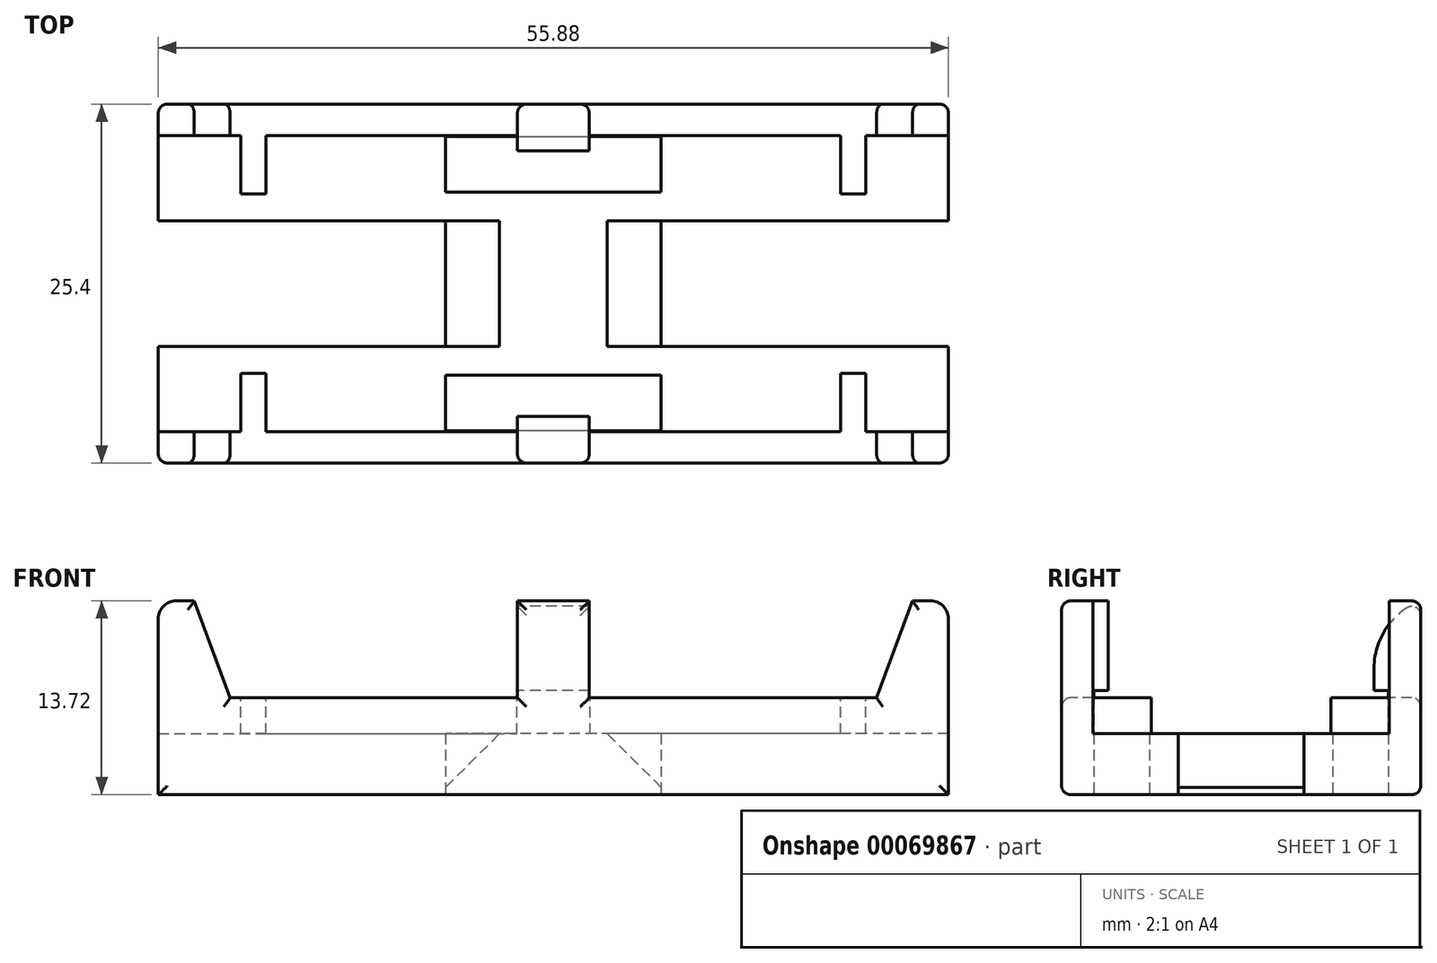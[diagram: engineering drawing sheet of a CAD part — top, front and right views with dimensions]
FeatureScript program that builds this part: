
annotation { "Feature Type Name" : "Feature", "Feature Type Description" : "" }
export const myFeature = defineFeature(function(context is Context, id is Id, definition is map)
    precondition{}
    {
        {
            var Q0;
            Q0=qCreatedBy(makeId("Top.planeOp"),FACE);
            var sketch = newSketch(context, id + "F0", { "sketchPlane" : qUnion([Q0])});
            skLineSegment(sketch, "E0.bottom", {"start": v(-27.94, 12.7) * mm, "end": v(27.94, 12.7) * mm});
            skLineSegment(sketch, "E0.top", {"start": v(-27.94, -12.7) * mm, "end": v(27.94, -12.7) * mm});
            skLineSegment(sketch, "E0.left", {"start": v(-27.94, 12.7) * mm, "end": v(-27.94, -12.7) * mm});
            skLineSegment(sketch, "E0.right", {"start": v(27.94, 12.7) * mm, "end": v(27.94, -12.7) * mm});
            skPoint(sketch, "E0.middle", {"position": v(0, 0) * mm});
            skSolve(sketch);
        }
        {
            var Q0;
            Q0=makeQuery(id+"F0.imprint","IMPRINT",FACE,{"disambiguationData":[TD([[makeQuery(id+"F0.imprint","IMPRINT",EDGE,{"derivedFrom":sQuery(id+"F0.wireOp",EDGE,"E0.bottom")}),-1.0]])]});
            extrude(context, id + "F1", {"entities" : qUnion([Q0]), "depth" : 13.72 * mm});
        }
        {
            var Q0;
            Q0=makeQuery(id+"F1.opExtrude","CAP_FACE",FACE,{"disambiguationData":[OSD([sQuery(id+"F0.wireOp",EDGE,"E0.bottom"),sQuery(id+"F0.wireOp",EDGE,"E0.top"),sQuery(id+"F0.wireOp",EDGE,"E0.left"),sQuery(id+"F0.wireOp",EDGE,"E0.right")])],"isStart":true});
            var sketch = newSketch(context, id + "F2", { "sketchPlane" : qUnion([Q0])});
            skLineSegment(sketch, "E1.bottom", {"start": v(27.94, 4.44) * mm, "end": v(7.62, 4.44) * mm});
            skLineSegment(sketch, "E1.top", {"start": v(27.94, -4.44) * mm, "end": v(7.62, -4.44) * mm});
            skLineSegment(sketch, "E1.left", {"start": v(27.94, 4.44) * mm, "end": v(27.94, -4.44) * mm});
            skLineSegment(sketch, "E1.right", {"start": v(7.62, 4.44) * mm, "end": v(7.62, -4.44) * mm});
            skSolve(sketch);
        }
        {
            var Q0;
            Q0 = qSketchRegion(id + "F2", true);
            extrude(context, id + "F3", {"entities" : qUnion([Q0]), "operationType" : NewBodyOperationType.REMOVE, "endBound" : BoundingType.THROUGH_ALL, "oppositeDirection" : true, "depth" : 25.4 * mm});
        }
        {
            var Q0;
            Q0=makeQuery(id+"F1.opExtrude","CAP_FACE",FACE,{"disambiguationData":[OSD([sQuery(id+"F0.wireOp",EDGE,"E0.bottom"),sQuery(id+"F0.wireOp",EDGE,"E0.top"),sQuery(id+"F0.wireOp",EDGE,"E0.left"),sQuery(id+"F0.wireOp",EDGE,"E0.right")])],"isStart":true});
            var sketch = newSketch(context, id + "F4", { "sketchPlane" : qUnion([Q0])});
            skLineSegment(sketch, "E2.bottom", {"start": v(-27.94, 4.45) * mm, "end": v(-7.62, 4.45) * mm});
            skLineSegment(sketch, "E2.top", {"start": v(-27.94, -4.44) * mm, "end": v(-7.62, -4.44) * mm});
            skLineSegment(sketch, "E2.left", {"start": v(-27.94, 4.45) * mm, "end": v(-27.94, -4.44) * mm});
            skLineSegment(sketch, "E2.right", {"start": v(-7.62, 4.45) * mm, "end": v(-7.62, -4.44) * mm});
            skSolve(sketch);
        }
        {
            var Q0;
            Q0 = qSketchRegion(id + "F4", true);
            extrude(context, id + "F5", {"entities" : qUnion([Q0]), "operationType" : NewBodyOperationType.REMOVE, "endBound" : BoundingType.THROUGH_ALL, "oppositeDirection" : true, "depth" : 25.4 * mm});
        }
        {
            var Q0;
            Q0=makeQuery(id+"F1.opExtrude","CAP_FACE",FACE,{"disambiguationData":[OSD([sQuery(id+"F0.wireOp",EDGE,"E0.bottom"),sQuery(id+"F0.wireOp",EDGE,"E0.top"),sQuery(id+"F0.wireOp",EDGE,"E0.left"),sQuery(id+"F0.wireOp",EDGE,"E0.right")])],"isStart":true});
            var sketch = newSketch(context, id + "F6", { "sketchPlane" : qUnion([Q0])});
            skLineSegment(sketch, "E3.bottom", {"start": v(7.62, 6.48) * mm, "end": v(-7.62, 6.48) * mm});
            skLineSegment(sketch, "E3.top", {"start": v(7.62, 10.41) * mm, "end": v(-7.62, 10.41) * mm});
            skLineSegment(sketch, "E3.left", {"start": v(7.62, 6.48) * mm, "end": v(7.62, 10.41) * mm});
            skLineSegment(sketch, "E3.right", {"start": v(-7.62, 6.48) * mm, "end": v(-7.62, 10.41) * mm});
            skPoint(sketch, "E3.middle", {"position": v(0, 8.45) * mm});
            skSolve(sketch);
        }
        {
            var Q0;
            Q0 = qSketchRegion(id + "F6", true);
            extrude(context, id + "F7", {"entities" : qUnion([Q0]), "operationType" : NewBodyOperationType.REMOVE, "oppositeDirection" : true, "depth" : 7.37 * mm});
        }
        {
            var Q0;
            Q0=makeQuery(id+"F1.opExtrude","CAP_FACE",FACE,{"disambiguationData":[OSD([sQuery(id+"F0.wireOp",EDGE,"E0.bottom"),sQuery(id+"F0.wireOp",EDGE,"E0.top"),sQuery(id+"F0.wireOp",EDGE,"E0.left"),sQuery(id+"F0.wireOp",EDGE,"E0.right")])],"isStart":true});
            var sketch = newSketch(context, id + "F8", { "sketchPlane" : qUnion([Q0])});
            skLineSegment(sketch, "E4.bottom", {"start": v(-7.62, -10.41) * mm, "end": v(7.62, -10.41) * mm});
            skLineSegment(sketch, "E4.top", {"start": v(-7.62, -6.48) * mm, "end": v(7.62, -6.48) * mm});
            skLineSegment(sketch, "E4.left", {"start": v(-7.62, -10.41) * mm, "end": v(-7.62, -6.48) * mm});
            skLineSegment(sketch, "E4.right", {"start": v(7.62, -10.41) * mm, "end": v(7.62, -6.48) * mm});
            skPoint(sketch, "E4.middle", {"position": v(0, -8.45) * mm});
            skSolve(sketch);
        }
        {
            var Q0;
            Q0 = qSketchRegion(id + "F8", true);
            var Q1;
            Q1=makeQuery(id+"F8.imprint","IMPRINT",FACE,{"disambiguationData":[TD([[makeQuery(id+"F8.imprint","IMPRINT",EDGE,{"derivedFrom":sQuery(id+"F8.wireOp",EDGE,"E4.bottom")}),1.0]])]});
            extrude(context, id + "F9", {"entities" : qUnion([Q0, Q1]), "operationType" : NewBodyOperationType.REMOVE, "oppositeDirection" : true, "depth" : 7.37 * mm});
        }
        {
            var Q0;
            Q0=makeQuery(id+"F1.opExtrude","CAP_FACE",FACE,{"disambiguationData":[OSD([sQuery(id+"F0.wireOp",EDGE,"E0.bottom"),sQuery(id+"F0.wireOp",EDGE,"E0.top"),sQuery(id+"F0.wireOp",EDGE,"E0.left"),sQuery(id+"F0.wireOp",EDGE,"E0.right")])],"isStart":false});
            var sketch = newSketch(context, id + "F10", { "sketchPlane" : qUnion([Q0])});
            skLineSegment(sketch, "E5.bottom", {"start": v(-27.94, 9.4) * mm, "end": v(27.94, 9.4) * mm});
            skLineSegment(sketch, "E5.top", {"start": v(-27.94, -9.4) * mm, "end": v(27.94, -9.4) * mm});
            skLineSegment(sketch, "E5.left", {"start": v(-27.94, 9.4) * mm, "end": v(-27.94, -9.4) * mm});
            skLineSegment(sketch, "E5.right", {"start": v(27.94, 9.4) * mm, "end": v(27.94, -9.4) * mm});
            skPoint(sketch, "E5.middle", {"position": v(0, 0) * mm});
            skSolve(sketch);
        }
        {
            var Q0;
            Q0 = qSketchRegion(id + "F10", true);
            extrude(context, id + "F11", {"entities" : qUnion([Q0]), "operationType" : NewBodyOperationType.REMOVE, "oppositeDirection" : true, "depth" : 9.4 * mm});
        }
        {
            var Q0;
            Q0=makeQuery(id+"F1.opExtrude","SWEPT_FACE",FACE,{"disambiguationData":[OSD([sQuery(id+"F0.wireOp",EDGE,"E0.top")])]});
            var sketch = newSketch(context, id + "F12", { "sketchPlane" : qUnion([Q0])});
            skLineSegment(sketch, "E6.bottom", {"start": v(-2.54, 13.72) * mm, "end": v(-22.86, 13.72) * mm});
            skLineSegment(sketch, "E6.top", {"start": v(-2.54, 6.86) * mm, "end": v(-22.86, 6.86) * mm});
            skLineSegment(sketch, "E6.left", {"start": v(-2.54, 13.72) * mm, "end": v(-2.54, 6.86) * mm});
            skLineSegment(sketch, "E6.right", {"start": v(-22.86, 13.72) * mm, "end": v(-22.86, 6.86) * mm});
            skSolve(sketch);
        }
        {
            var Q0;
            Q0 = qSketchRegion(id + "F12", true);
            extrude(context, id + "F13", {"entities" : qUnion([Q0]), "operationType" : NewBodyOperationType.REMOVE, "endBound" : BoundingType.THROUGH_ALL, "oppositeDirection" : true, "depth" : 25.4 * mm});
        }
        {
            var Q0;
            Q0=makeQuery(id+"F1.opExtrude","SWEPT_FACE",FACE,{"disambiguationData":[OSD([sQuery(id+"F0.wireOp",EDGE,"E0.top")])]});
            var sketch = newSketch(context, id + "F14", { "sketchPlane" : qUnion([Q0])});
            skLineSegment(sketch, "E7.bottom", {"start": v(22.86, 13.72) * mm, "end": v(2.54, 13.72) * mm});
            skLineSegment(sketch, "E7.top", {"start": v(22.86, 6.86) * mm, "end": v(2.54, 6.86) * mm});
            skLineSegment(sketch, "E7.left", {"start": v(22.86, 13.72) * mm, "end": v(22.86, 6.86) * mm});
            skLineSegment(sketch, "E7.right", {"start": v(2.54, 13.72) * mm, "end": v(2.54, 6.86) * mm});
            skSolve(sketch);
        }
        {
            var Q0;
            Q0 = qSketchRegion(id + "F14", true);
            extrude(context, id + "F15", {"entities" : qUnion([Q0]), "operationType" : NewBodyOperationType.REMOVE, "endBound" : BoundingType.THROUGH_ALL, "oppositeDirection" : true, "depth" : 25.4 * mm});
        }
        {
            var Q0;
            Q0=makeQuery(id+"F1.opExtrude","SWEPT_FACE",FACE,{"disambiguationData":[OSD([sQuery(id+"F0.wireOp",EDGE,"E0.top")])]});
            var sketch = newSketch(context, id + "F16", { "sketchPlane" : qUnion([Q0])});
            skLineSegment(sketch, "E8", {"start": v(-22.86, 6.86) * mm, "end": v(-25.4, 13.72) * mm});
            skSolve(sketch);
        }
        {
            var Q0;
            {var subQ0=sQuery(id+"F16.wireOp",EDGE,"E8");Q0=makeQuery(id+"F16.imprint","IMPRINT",FACE,{"disambiguationData":[TD([[makeQuery(id+"F16.imprint","IMPRINT",EDGE,{"derivedFrom":subQ0}),-1.0]])]});}
            extrude(context, id + "F17", {"entities" : qUnion([Q0]), "operationType" : NewBodyOperationType.REMOVE, "endBound" : BoundingType.THROUGH_ALL, "oppositeDirection" : true, "depth" : 25.4 * mm});
        }
        {
            var Q0;
            Q0=makeQuery(id+"F1.opExtrude","SWEPT_FACE",FACE,{"disambiguationData":[OSD([sQuery(id+"F0.wireOp",EDGE,"E0.top")])]});
            var sketch = newSketch(context, id + "F18", { "sketchPlane" : qUnion([Q0])});
            skLineSegment(sketch, "E9", {"start": v(22.86, 6.86) * mm, "end": v(25.4, 13.72) * mm});
            skLineSegment(sketch, "E10", {"start": v(25.4, 13.72) * mm, "end": v(22.86, 13.72) * mm});
            skLineSegment(sketch, "E11", {"start": v(22.86, 13.72) * mm, "end": v(22.86, 6.86) * mm});
            skSolve(sketch);
        }
        {
            var Q0;
            Q0 = qSketchRegion(id + "F18", true);
            extrude(context, id + "F19", {"entities" : qUnion([Q0]), "operationType" : NewBodyOperationType.REMOVE, "endBound" : BoundingType.THROUGH_ALL, "oppositeDirection" : true, "depth" : 25.4 * mm});
        }
        {
            var Q0;
            Q0=makeQuery(id+"F17.boolean.opBoolean","COPY",EDGE,{"disambiguationData":[OD(1.0)],"derivedFrom":makeQuery(id+"F17.opExtrude","SWEPT_EDGE",EDGE,{"disambiguationData":[OSD([sQuery(id+"F0.wireOp",EDGE,"E0.top"),sQuery(id+"F16.wireOp",EDGE,"E8")])]})});
            var Q1;
            Q1=makeQuery(id+"F17.boolean.opBoolean","COPY",EDGE,{"disambiguationData":[OD(0.0)],"derivedFrom":makeQuery(id+"F17.opExtrude","SWEPT_EDGE",EDGE,{"disambiguationData":[OSD([sQuery(id+"F0.wireOp",EDGE,"E0.top"),sQuery(id+"F16.wireOp",EDGE,"E8")])]})});
            var Q2;
            Q2=makeQuery(id+"F19.boolean.opBoolean","COPY",EDGE,{"disambiguationData":[OD(1.0)],"derivedFrom":makeQuery(id+"F19.opExtrude","SWEPT_EDGE",EDGE,{"disambiguationData":[OSD([sQuery(id+"F0.wireOp",EDGE,"E0.top"),sQuery(id+"F18.wireOp",EDGE,"E9"),sQuery(id+"F18.wireOp",EDGE,"E10")])]})});
            var Q3;
            Q3=makeQuery(id+"F19.boolean.opBoolean","COPY",EDGE,{"disambiguationData":[OD(0.0)],"derivedFrom":makeQuery(id+"F19.opExtrude","SWEPT_EDGE",EDGE,{"disambiguationData":[OSD([sQuery(id+"F0.wireOp",EDGE,"E0.top"),sQuery(id+"F18.wireOp",EDGE,"E9"),sQuery(id+"F18.wireOp",EDGE,"E10")])]})});
            var Q4;
            {var subQ0=sQuery(id+"F0.wireOp",EDGE,"E0.bottom");var subQ1=sQuery(id+"F0.wireOp",EDGE,"E0.left");Q4=makeQuery(id+"F5.boolean.opBoolean","SPLIT",EDGE,{"disambiguationData":[TD([makeQuery(id+"F1.opExtrude","SWEPT_FACE",FACE,{"disambiguationData":[OSD([subQ0])]})])],"derivedFrom":makeQuery(id+"F1.opExtrude","CAP_EDGE",EDGE,{"disambiguationData":[OSD([subQ1])],"isStart":false})});}
            var Q5;
            {var subQ0=sQuery(id+"F0.wireOp",EDGE,"E0.left");var subQ1=sQuery(id+"F0.wireOp",EDGE,"E0.top");Q5=makeQuery(id+"F5.boolean.opBoolean","SPLIT",EDGE,{"disambiguationData":[TD([makeQuery(id+"F1.opExtrude","SWEPT_FACE",FACE,{"disambiguationData":[OSD([subQ1])]})])],"derivedFrom":makeQuery(id+"F1.opExtrude","CAP_EDGE",EDGE,{"disambiguationData":[OSD([subQ0])],"isStart":false})});}
            var Q6;
            {var subQ0=sQuery(id+"F0.wireOp",EDGE,"E0.right");var subQ1=sQuery(id+"F0.wireOp",EDGE,"E0.top");Q6=makeQuery(id+"F3.boolean.opBoolean","SPLIT",EDGE,{"disambiguationData":[TD([makeQuery(id+"F1.opExtrude","SWEPT_FACE",FACE,{"disambiguationData":[OSD([subQ1])]})])],"derivedFrom":makeQuery(id+"F1.opExtrude","CAP_EDGE",EDGE,{"disambiguationData":[OSD([subQ0])],"isStart":false})});}
            var Q7;
            {var subQ0=sQuery(id+"F0.wireOp",EDGE,"E0.bottom");var subQ1=sQuery(id+"F0.wireOp",EDGE,"E0.right");Q7=makeQuery(id+"F3.boolean.opBoolean","SPLIT",EDGE,{"disambiguationData":[TD([makeQuery(id+"F1.opExtrude","SWEPT_FACE",FACE,{"disambiguationData":[OSD([subQ0])]})])],"derivedFrom":makeQuery(id+"F1.opExtrude","CAP_EDGE",EDGE,{"disambiguationData":[OSD([subQ1])],"isStart":false})});}
            fillet(context, id + "F20", {"entities" : qUnion([Q0, Q1, Q2, Q3, Q4, Q5, Q6, Q7]), "radius" : 1.27 * mm, "tangentPropagation" : true, "allowEdgeOverflow" : false});
        }
        {
            var Q0;
            {var subQ0=sQuery(id+"F0.wireOp",EDGE,"E0.bottom");var subQ1=makeQuery(id+"F1.opExtrude","SWEPT_FACE",FACE,{"disambiguationData":[OSD([subQ0])]});var subQ3=sQuery(id+"F0.wireOp",EDGE,"E0.left");var subQ4=makeQuery(id+"F1.opExtrude","SWEPT_FACE",FACE,{"disambiguationData":[OSD([subQ3])]});var subQ5=sQuery(id+"F0.wireOp",EDGE,"E0.right");Q0=makeQuery(id+"F13.boolean.opBoolean","SPLIT",FACE,{"disambiguationData":[TD([subQ4])],"derivedFrom":makeQuery(id+"F11.boolean.opBoolean","SPLIT",FACE,{"disambiguationData":[TD([subQ1])],"derivedFrom":makeQuery(id+"F1.opExtrude","CAP_FACE",FACE,{"disambiguationData":[OSD([subQ0,sQuery(id+"F0.wireOp",EDGE,"E0.top"),subQ3,subQ5])],"isStart":false})})});}
            var sketch = newSketch(context, id + "F21", { "sketchPlane" : qUnion([Q0])});
            skLineSegment(sketch, "E12.bottom", {"start": v(-40.66, 10.48) * mm, "end": v(-2.56, 10.48) * mm});
            skLineSegment(sketch, "E12.top", {"start": v(-40.66, -10.48) * mm, "end": v(-2.56, -10.48) * mm});
            skLineSegment(sketch, "E12.left", {"start": v(-40.66, 10.48) * mm, "end": v(-40.66, -10.48) * mm});
            skLineSegment(sketch, "E12.right", {"start": v(-2.56, 10.48) * mm, "end": v(-2.56, -10.48) * mm});
            skPoint(sketch, "E12.middle", {"position": v(-21.61, 0) * mm});
            skSolve(sketch);
        }
        {
            var Q0;
            Q0 = qSketchRegion(id + "F21", true);
            extrude(context, id + "F22", {"entities" : qUnion([Q0]), "operationType" : NewBodyOperationType.REMOVE, "oppositeDirection" : true, "depth" : 9.4 * mm});
        }
        {
            var Q0;
            {var subQ0=sQuery(id+"F0.wireOp",EDGE,"E0.bottom");var subQ1=makeQuery(id+"F1.opExtrude","SWEPT_FACE",FACE,{"disambiguationData":[OSD([subQ0])]});var subQ4=sQuery(id+"F0.wireOp",EDGE,"E0.right");var subQ5=makeQuery(id+"F1.opExtrude","SWEPT_FACE",FACE,{"disambiguationData":[OSD([subQ4])]});var subQ6=sQuery(id+"F0.wireOp",EDGE,"E0.left");Q0=makeQuery(id+"F15.boolean.opBoolean","SPLIT",FACE,{"disambiguationData":[TD([subQ5])],"derivedFrom":makeQuery(id+"F13.boolean.opBoolean","SPLIT",FACE,{"disambiguationData":[TD([subQ5])],"derivedFrom":makeQuery(id+"F11.boolean.opBoolean","SPLIT",FACE,{"disambiguationData":[TD([subQ1])],"derivedFrom":makeQuery(id+"F1.opExtrude","CAP_FACE",FACE,{"disambiguationData":[OSD([subQ0,sQuery(id+"F0.wireOp",EDGE,"E0.top"),subQ6,subQ4])],"isStart":false})})})});}
            var sketch = newSketch(context, id + "F23", { "sketchPlane" : qUnion([Q0])});
            skLineSegment(sketch, "E13.bottom", {"start": v(40.7, 10.48) * mm, "end": v(2.6, 10.48) * mm});
            skLineSegment(sketch, "E13.top", {"start": v(40.7, -10.48) * mm, "end": v(2.6, -10.48) * mm});
            skLineSegment(sketch, "E13.left", {"start": v(40.7, 10.48) * mm, "end": v(40.7, -10.48) * mm});
            skLineSegment(sketch, "E13.right", {"start": v(2.6, 10.48) * mm, "end": v(2.6, -10.48) * mm});
            skPoint(sketch, "E13.middle", {"position": v(21.64, 0) * mm});
            skSolve(sketch);
        }
        {
            var Q0;
            Q0 = qSketchRegion(id + "F23", true);
            extrude(context, id + "F24", {"entities" : qUnion([Q0]), "operationType" : NewBodyOperationType.REMOVE, "oppositeDirection" : true, "depth" : 9.4 * mm});
        }
        {
            var Q0;
            {var subQ0=sQuery(id+"F0.wireOp",EDGE,"E0.right");var subQ2=sQuery(id+"F10.wireOp",EDGE,"E5.bottom");var subQ4=makeQuery(id+"F13.opExtrude","SWEPT_FACE",FACE,{"disambiguationData":[OSD([sQuery(id+"F12.wireOp",EDGE,"E6.left")])]});Q0=makeQuery(id+"F15.boolean.opBoolean","SPLIT",EDGE,{"disambiguationData":[TD([makeQuery(id+"F13.boolean.opBoolean","COPY",FACE,{"disambiguationData":[OD(1.0)],"derivedFrom":subQ4})])],"derivedFrom":makeQuery(id+"F13.boolean.opBoolean","SPLIT",EDGE,{"disambiguationData":[TD([makeQuery(id+"F1.opExtrude","SWEPT_FACE",FACE,{"disambiguationData":[OSD([subQ0])]})])],"derivedFrom":makeQuery(id+"F11.boolean.opBoolean","COPY",EDGE,{"derivedFrom":makeQuery(id+"F11.opExtrude","CAP_EDGE",EDGE,{"disambiguationData":[OSD([subQ2])],"isStart":true})})})});}
            var Q1;
            {var subQ0=sQuery(id+"F0.wireOp",EDGE,"E0.right");var subQ2=sQuery(id+"F10.wireOp",EDGE,"E5.top");var subQ4=makeQuery(id+"F13.opExtrude","SWEPT_FACE",FACE,{"disambiguationData":[OSD([sQuery(id+"F12.wireOp",EDGE,"E6.left")])]});Q1=makeQuery(id+"F15.boolean.opBoolean","SPLIT",EDGE,{"disambiguationData":[TD([makeQuery(id+"F13.boolean.opBoolean","COPY",FACE,{"disambiguationData":[OD(0.0)],"derivedFrom":subQ4})])],"derivedFrom":makeQuery(id+"F13.boolean.opBoolean","SPLIT",EDGE,{"disambiguationData":[TD([makeQuery(id+"F1.opExtrude","SWEPT_FACE",FACE,{"disambiguationData":[OSD([subQ0])]})])],"derivedFrom":makeQuery(id+"F11.boolean.opBoolean","COPY",EDGE,{"derivedFrom":makeQuery(id+"F11.opExtrude","CAP_EDGE",EDGE,{"disambiguationData":[OSD([subQ2])],"isStart":true})})})});}
            fillet(context, id + "F25", {"entities" : qUnion([Q0, Q1]), "radius" : 5.08 * mm, "tangentPropagation" : true, "allowEdgeOverflow" : false});
        }
        {
            var Q0;
            Q0=makeQuery(id+"F24.boolean.opBoolean","MERGE",FACE,{"derivedFrom":[makeQuery(id+"F22.boolean.opBoolean","MERGE",FACE,{"derivedFrom":[makeQuery(id+"F11.boolean.opBoolean","COPY",FACE,{"derivedFrom":makeQuery(id+"F11.opExtrude","CAP_FACE",FACE,{"disambiguationData":[OSD([sQuery(id+"F10.wireOp",EDGE,"E5.bottom"),sQuery(id+"F10.wireOp",EDGE,"E5.top"),sQuery(id+"F10.wireOp",EDGE,"E5.left"),sQuery(id+"F10.wireOp",EDGE,"E5.right")])],"isStart":false})}),makeQuery(id+"F22.opExtrude","CAP_FACE",FACE,{"disambiguationData":[OSD([sQuery(id+"F21.wireOp",EDGE,"E12.bottom"),sQuery(id+"F21.wireOp",EDGE,"E12.top"),sQuery(id+"F21.wireOp",EDGE,"E12.left"),sQuery(id+"F21.wireOp",EDGE,"E12.right")])],"isStart":false})]}),makeQuery(id+"F24.opExtrude","CAP_FACE",FACE,{"disambiguationData":[OSD([sQuery(id+"F23.wireOp",EDGE,"E13.bottom"),sQuery(id+"F23.wireOp",EDGE,"E13.top"),sQuery(id+"F23.wireOp",EDGE,"E13.left"),sQuery(id+"F23.wireOp",EDGE,"E13.right")])],"isStart":false})]});
            var sketch = newSketch(context, id + "F26", { "sketchPlane" : qUnion([Q0])});
            skLineSegment(sketch, "E14.bottom", {"start": v(20.32, 10.48) * mm, "end": v(22.1, 10.48) * mm});
            skLineSegment(sketch, "E14.top", {"start": v(20.32, -10.48) * mm, "end": v(22.1, -10.48) * mm});
            skLineSegment(sketch, "E14.left", {"start": v(20.32, 10.48) * mm, "end": v(20.32, -10.48) * mm});
            skLineSegment(sketch, "E14.right", {"start": v(22.1, 10.48) * mm, "end": v(22.1, -10.48) * mm});
            skPoint(sketch, "E14.middle", {"position": v(21.2, 0) * mm});
            skSolve(sketch);
        }
        {
            var Q0;
            Q0 = qSketchRegion(id + "F26", true);
            extrude(context, id + "F27", {"entities" : qUnion([Q0]), "operationType" : NewBodyOperationType.ADD, "depth" : 2.54 * mm});
        }
        {
            var Q0;
            {var subQ0=sQuery(id+"F23.wireOp",EDGE,"E13.right");var subQ1=makeQuery(id+"F24.opExtrude","SWEPT_FACE",FACE,{"disambiguationData":[OSD([subQ0])]});var subQ2=sQuery(id+"F23.wireOp",EDGE,"E13.bottom");var subQ3=sQuery(id+"F21.wireOp",EDGE,"E12.right");var subQ4=makeQuery(id+"F22.opExtrude","SWEPT_FACE",FACE,{"disambiguationData":[OSD([subQ3])]});var subQ5=sQuery(id+"F21.wireOp",EDGE,"E12.bottom");var subQ6=sQuery(id+"F21.wireOp",EDGE,"E12.top");var subQ7=sQuery(id+"F23.wireOp",EDGE,"E13.top");var subQ8=sQuery(id+"F26.wireOp",EDGE,"E14.left");Q0=makeQuery(id+"F27.boolean.opBoolean","SPLIT",FACE,{"disambiguationData":[TD([makeQuery(id+"F1.opExtrude","SWEPT_FACE",FACE,{"disambiguationData":[OSD([sQuery(id+"F0.wireOp",EDGE,"E0.left")])]}),makeQuery(id+"F3.boolean.opBoolean","COPY",FACE,{"derivedFrom":makeQuery(id+"F3.opExtrude","SWEPT_FACE",FACE,{"disambiguationData":[OSD([sQuery(id+"F2.wireOp",EDGE,"E1.bottom")])]})}),makeQuery(id+"F3.boolean.opBoolean","COPY",FACE,{"derivedFrom":makeQuery(id+"F3.opExtrude","SWEPT_FACE",FACE,{"disambiguationData":[OSD([sQuery(id+"F2.wireOp",EDGE,"E1.top")])]})}),makeQuery(id+"F3.boolean.opBoolean","COPY",FACE,{"derivedFrom":makeQuery(id+"F3.opExtrude","SWEPT_FACE",FACE,{"disambiguationData":[OSD([sQuery(id+"F2.wireOp",EDGE,"E1.right")])]})}),makeQuery(id+"F5.boolean.opBoolean","COPY",FACE,{"derivedFrom":makeQuery(id+"F5.opExtrude","SWEPT_FACE",FACE,{"disambiguationData":[OSD([sQuery(id+"F4.wireOp",EDGE,"E2.bottom")])]})}),makeQuery(id+"F5.boolean.opBoolean","COPY",FACE,{"derivedFrom":makeQuery(id+"F5.opExtrude","SWEPT_FACE",FACE,{"disambiguationData":[OSD([sQuery(id+"F4.wireOp",EDGE,"E2.top")])]})}),makeQuery(id+"F5.boolean.opBoolean","COPY",FACE,{"derivedFrom":makeQuery(id+"F5.opExtrude","SWEPT_FACE",FACE,{"disambiguationData":[OSD([sQuery(id+"F4.wireOp",EDGE,"E2.right")])]})}),makeQuery(id+"F7.boolean.opBoolean","COPY",FACE,{"derivedFrom":makeQuery(id+"F7.opExtrude","SWEPT_FACE",FACE,{"disambiguationData":[OSD([sQuery(id+"F6.wireOp",EDGE,"E3.bottom")])]})}),makeQuery(id+"F7.boolean.opBoolean","COPY",FACE,{"derivedFrom":makeQuery(id+"F7.opExtrude","SWEPT_FACE",FACE,{"disambiguationData":[OSD([sQuery(id+"F6.wireOp",EDGE,"E3.top")])]})}),makeQuery(id+"F7.boolean.opBoolean","COPY",FACE,{"derivedFrom":makeQuery(id+"F7.opExtrude","SWEPT_FACE",FACE,{"disambiguationData":[OSD([sQuery(id+"F6.wireOp",EDGE,"E3.left")])]})}),makeQuery(id+"F7.boolean.opBoolean","COPY",FACE,{"derivedFrom":makeQuery(id+"F7.opExtrude","SWEPT_FACE",FACE,{"disambiguationData":[OSD([sQuery(id+"F6.wireOp",EDGE,"E3.right")])]})}),makeQuery(id+"F9.boolean.opBoolean","COPY",FACE,{"derivedFrom":makeQuery(id+"F9.opExtrude","SWEPT_FACE",FACE,{"disambiguationData":[OSD([sQuery(id+"F8.wireOp",EDGE,"E4.bottom")])]})}),makeQuery(id+"F9.boolean.opBoolean","COPY",FACE,{"derivedFrom":makeQuery(id+"F9.opExtrude","SWEPT_FACE",FACE,{"disambiguationData":[OSD([sQuery(id+"F8.wireOp",EDGE,"E4.top")])]})}),makeQuery(id+"F9.boolean.opBoolean","COPY",FACE,{"derivedFrom":makeQuery(id+"F9.opExtrude","SWEPT_FACE",FACE,{"disambiguationData":[OSD([sQuery(id+"F8.wireOp",EDGE,"E4.left")])]})}),makeQuery(id+"F9.boolean.opBoolean","COPY",FACE,{"derivedFrom":makeQuery(id+"F9.opExtrude","SWEPT_FACE",FACE,{"disambiguationData":[OSD([sQuery(id+"F8.wireOp",EDGE,"E4.right")])]})}),makeQuery(id+"F22.boolean.opBoolean","COPY",FACE,{"derivedFrom":makeQuery(id+"F22.opExtrude","SWEPT_FACE",FACE,{"disambiguationData":[OSD([subQ5])]})}),makeQuery(id+"F22.boolean.opBoolean","COPY",FACE,{"derivedFrom":makeQuery(id+"F22.opExtrude","SWEPT_FACE",FACE,{"disambiguationData":[OSD([subQ6])]})}),makeQuery(id+"F22.boolean.opBoolean","COPY",FACE,{"disambiguationData":[OD(0.0)],"derivedFrom":subQ4}),makeQuery(id+"F22.boolean.opBoolean","COPY",FACE,{"disambiguationData":[OD(1.0)],"derivedFrom":subQ4}),makeQuery(id+"F24.boolean.opBoolean","COPY",FACE,{"derivedFrom":makeQuery(id+"F24.opExtrude","SWEPT_FACE",FACE,{"disambiguationData":[OSD([subQ2])]})}),makeQuery(id+"F24.boolean.opBoolean","COPY",FACE,{"derivedFrom":makeQuery(id+"F24.opExtrude","SWEPT_FACE",FACE,{"disambiguationData":[OSD([subQ7])]})}),makeQuery(id+"F24.boolean.opBoolean","COPY",FACE,{"disambiguationData":[OD(0.0)],"derivedFrom":subQ1}),makeQuery(id+"F24.boolean.opBoolean","COPY",FACE,{"disambiguationData":[OD(1.0)],"derivedFrom":subQ1}),makeQuery(id+"F27.opExtrude","CAP_FACE",FACE,{"disambiguationData":[OSD([sQuery(id+"F26.wireOp",EDGE,"E14.bottom"),sQuery(id+"F26.wireOp",EDGE,"E14.top"),subQ8,sQuery(id+"F26.wireOp",EDGE,"E14.right")])],"isStart":true}),makeQuery(id+"F27.opExtrude","SWEPT_FACE",FACE,{"disambiguationData":[OSD([subQ8])]})])],"derivedFrom":makeQuery(id+"F24.boolean.opBoolean","MERGE",FACE,{"derivedFrom":[makeQuery(id+"F22.boolean.opBoolean","MERGE",FACE,{"derivedFrom":[makeQuery(id+"F11.boolean.opBoolean","COPY",FACE,{"derivedFrom":makeQuery(id+"F11.opExtrude","CAP_FACE",FACE,{"disambiguationData":[OSD([sQuery(id+"F10.wireOp",EDGE,"E5.bottom"),sQuery(id+"F10.wireOp",EDGE,"E5.top"),sQuery(id+"F10.wireOp",EDGE,"E5.left"),sQuery(id+"F10.wireOp",EDGE,"E5.right")])],"isStart":false})}),makeQuery(id+"F22.opExtrude","CAP_FACE",FACE,{"disambiguationData":[OSD([subQ5,subQ6,sQuery(id+"F21.wireOp",EDGE,"E12.left"),subQ3])],"isStart":false})]}),makeQuery(id+"F24.opExtrude","CAP_FACE",FACE,{"disambiguationData":[OSD([subQ2,subQ7,sQuery(id+"F23.wireOp",EDGE,"E13.left"),subQ0])],"isStart":false})]})});}
            var sketch = newSketch(context, id + "F28", { "sketchPlane" : qUnion([Q0])});
            skLineSegment(sketch, "E15.bottom", {"start": v(-22.1, 10.48) * mm, "end": v(-20.32, 10.48) * mm});
            skLineSegment(sketch, "E15.top", {"start": v(-22.1, -10.48) * mm, "end": v(-20.32, -10.48) * mm});
            skLineSegment(sketch, "E15.left", {"start": v(-22.1, 10.48) * mm, "end": v(-22.1, -10.48) * mm});
            skLineSegment(sketch, "E15.right", {"start": v(-20.32, 10.48) * mm, "end": v(-20.32, -10.48) * mm});
            skPoint(sketch, "E15.middle", {"position": v(-21.2, 0) * mm});
            skSolve(sketch);
        }
        {
            var Q0;
            Q0 = qSketchRegion(id + "F28", true);
            extrude(context, id + "F29", {"entities" : qUnion([Q0]), "operationType" : NewBodyOperationType.ADD, "depth" : 2.54 * mm});
        }
        {
            var Q0;
            Q0=makeQuery(id+"F29.opExtrude","CAP_FACE",FACE,{"disambiguationData":[OSD([sQuery(id+"F28.wireOp",EDGE,"E15.bottom"),sQuery(id+"F28.wireOp",EDGE,"E15.top"),sQuery(id+"F28.wireOp",EDGE,"E15.left"),sQuery(id+"F28.wireOp",EDGE,"E15.right")])],"isStart":false});
            var sketch = newSketch(context, id + "F30", { "sketchPlane" : qUnion([Q0])});
            skLineSegment(sketch, "E16.bottom", {"start": v(27.78, -6.35) * mm, "end": v(-28.1, -6.35) * mm});
            skLineSegment(sketch, "E16.top", {"start": v(27.78, 6.35) * mm, "end": v(-28.1, 6.35) * mm});
            skLineSegment(sketch, "E16.left", {"start": v(27.78, -6.35) * mm, "end": v(27.78, 6.35) * mm});
            skLineSegment(sketch, "E16.right", {"start": v(-28.1, -6.35) * mm, "end": v(-28.1, 6.35) * mm});
            skPoint(sketch, "E16.middle", {"position": v(-0.16, 0) * mm});
            skPoint(sketch, "E16.middle.positionSnap0", {"position": v(-20.32, 0) * mm});
            skPoint(sketch, "E16.centerSnap0", {"position": v(-20.32, 0) * mm});
            skSolve(sketch);
        }
        {
            var Q0;
            Q0 = qSketchRegion(id + "F30", true);
            extrude(context, id + "F31", {"entities" : qUnion([Q0]), "operationType" : NewBodyOperationType.REMOVE, "oppositeDirection" : true, "depth" : 2.54 * mm});
        }
        {
            var Q0;
            Q0=makeQuery(id+"F11.boolean.opBoolean","INTERSECT",EDGE,{"derivedFrom":[makeQuery(id+"F3.boolean.opBoolean","COPY",FACE,{"derivedFrom":makeQuery(id+"F3.opExtrude","SWEPT_FACE",FACE,{"disambiguationData":[OSD([sQuery(id+"F2.wireOp",EDGE,"E1.right")])]})}),makeQuery(id+"F11.opExtrude","CAP_FACE",FACE,{"disambiguationData":[OSD([sQuery(id+"F10.wireOp",EDGE,"E5.bottom"),sQuery(id+"F10.wireOp",EDGE,"E5.top"),sQuery(id+"F10.wireOp",EDGE,"E5.left"),sQuery(id+"F10.wireOp",EDGE,"E5.right")])],"isStart":false})]});
            var Q1;
            Q1=makeQuery(id+"F11.boolean.opBoolean","INTERSECT",EDGE,{"derivedFrom":[makeQuery(id+"F5.boolean.opBoolean","COPY",FACE,{"derivedFrom":makeQuery(id+"F5.opExtrude","SWEPT_FACE",FACE,{"disambiguationData":[OSD([sQuery(id+"F4.wireOp",EDGE,"E2.right")])]})}),makeQuery(id+"F11.opExtrude","CAP_FACE",FACE,{"disambiguationData":[OSD([sQuery(id+"F10.wireOp",EDGE,"E5.bottom"),sQuery(id+"F10.wireOp",EDGE,"E5.top"),sQuery(id+"F10.wireOp",EDGE,"E5.left"),sQuery(id+"F10.wireOp",EDGE,"E5.right")])],"isStart":false})]});
            chamfer(context, id + "F32", {"entities" : qUnion([Q0, Q1]), "width" : 3.8 * mm, "tangentPropagation" : true});
        }
        {
            var Q0;
            Q0=makeQuery(id+"F1.opExtrude","SWEPT_FACE",FACE,{"disambiguationData":[OSD([sQuery(id+"F0.wireOp",EDGE,"E0.top")])]});
            var Q1;
            Q1=makeQuery(id+"F1.opExtrude","SWEPT_FACE",FACE,{"disambiguationData":[OSD([sQuery(id+"F0.wireOp",EDGE,"E0.bottom")])]});
            fillet(context, id + "F33", {"entities" : qUnion([Q0, Q1]), "radius" : 0.64 * mm, "tangentPropagation" : true, "allowEdgeOverflow" : false});
        }
    });
